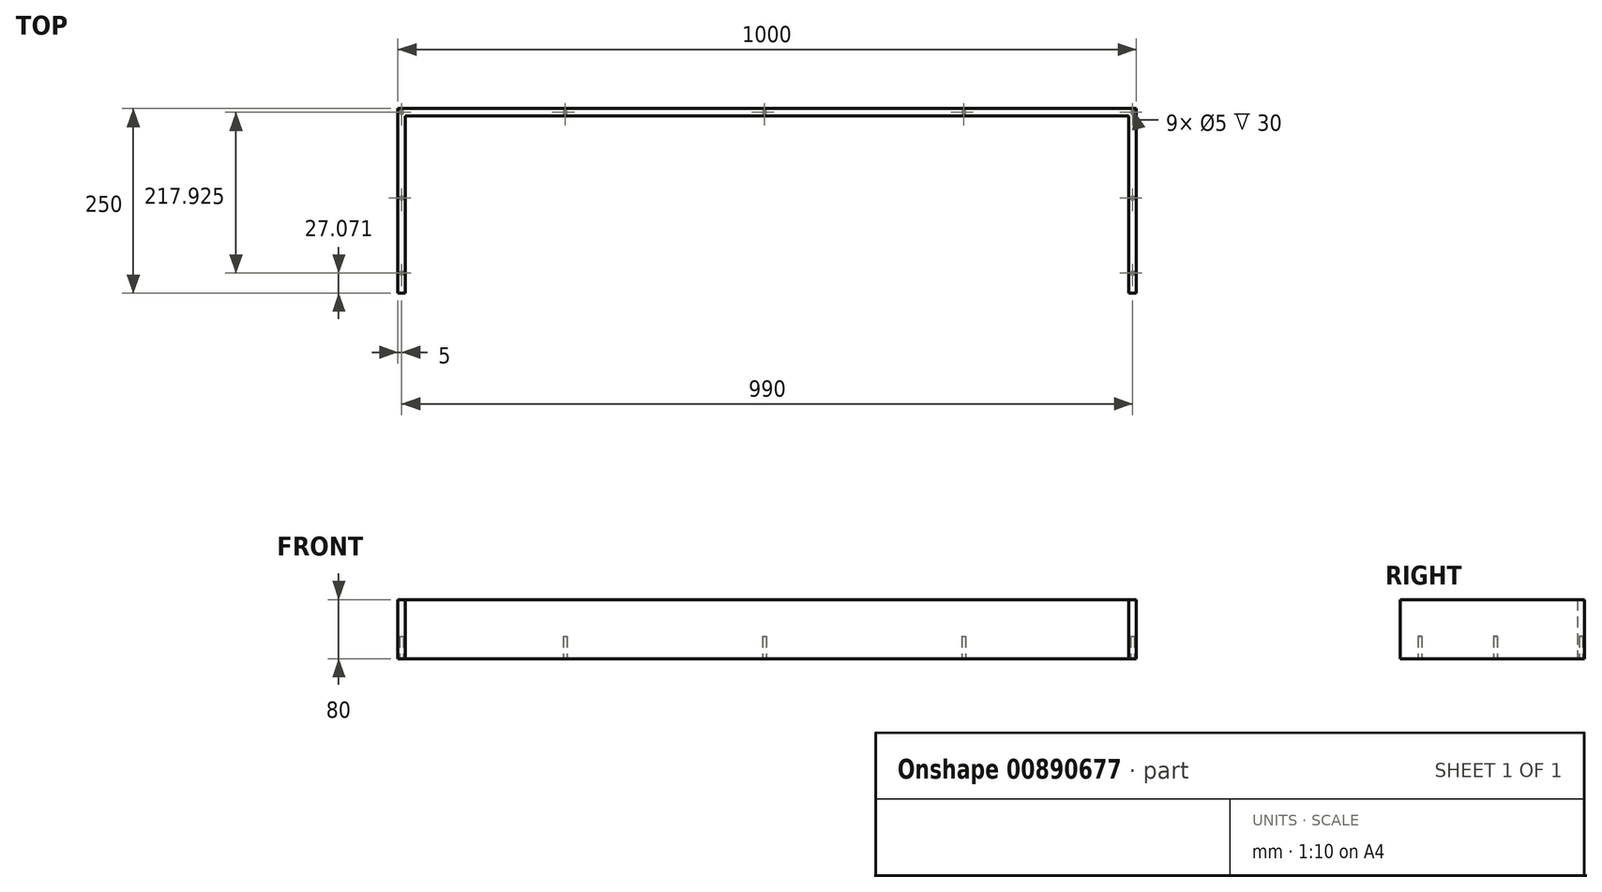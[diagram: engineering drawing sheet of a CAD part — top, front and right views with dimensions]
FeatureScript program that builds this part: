
annotation { "Feature Type Name" : "Feature", "Feature Type Description" : "" }
export const myFeature = defineFeature(function(context is Context, id is Id, definition is map)
    precondition{}
    {
        {
            var Q0;
            Q0=qCreatedBy(makeId("Top.planeOp"),FACE);
            var sketch = newSketch(context, id + "F0", { "sketchPlane" : qUnion([Q0])});
            skLineSegment(sketch, "E0.bottom", {"start": v(-496.42, 69.09) * mm, "end": v(503.58, 69.09) * mm});
            skLineSegment(sketch, "E0.top", {"start": v(-496.42, 59.09) * mm, "end": v(503.58, 59.09) * mm});
            skLineSegment(sketch, "E0.left", {"start": v(-496.42, 69.09) * mm, "end": v(-496.42, 59.09) * mm});
            skLineSegment(sketch, "E0.right", {"start": v(503.58, 69.09) * mm, "end": v(503.58, 59.09) * mm});
            skLineSegment(sketch, "E1.bottom", {"start": v(-496.42, 69.09) * mm, "end": v(-486.42, 69.09) * mm});
            skLineSegment(sketch, "E1.top", {"start": v(-496.42, -180.91) * mm, "end": v(-486.42, -180.91) * mm});
            skLineSegment(sketch, "E1.left", {"start": v(-496.42, 69.09) * mm, "end": v(-496.42, -180.91) * mm});
            skLineSegment(sketch, "E1.right", {"start": v(-486.42, 69.09) * mm, "end": v(-486.42, -180.91) * mm});
            skLineSegment(sketch, "E2.bottom", {"start": v(503.58, 69.09) * mm, "end": v(493.58, 69.09) * mm});
            skLineSegment(sketch, "E2.top", {"start": v(503.58, -180.91) * mm, "end": v(493.58, -180.91) * mm});
            skLineSegment(sketch, "E2.left", {"start": v(503.58, 69.09) * mm, "end": v(503.58, -180.91) * mm});
            skLineSegment(sketch, "E2.right", {"start": v(493.58, 69.09) * mm, "end": v(493.58, -180.91) * mm});
            skSolve(sketch);
        }
        {
            var Q0;
            Q0 = qSketchRegion(id + "F0", true);
            extrude(context, id + "F1", {"entities" : qUnion([Q0]), "depth" : 80 * mm, "offsetDistance" : 25 * mm});
        }
        {
            var Q0;
            Q0=makeQuery(id+"F1.opExtrude","CAP_FACE",FACE,{"disambiguationData":[OSD([sQuery(id+"F0.wireOp",EDGE,"E0.bottom"),sQuery(id+"F0.wireOp",EDGE,"E0.top"),sQuery(id+"F0.wireOp",EDGE,"E1.bottom"),sQuery(id+"F0.wireOp",EDGE,"E1.top"),sQuery(id+"F0.wireOp",EDGE,"E1.left"),sQuery(id+"F0.wireOp",EDGE,"E1.right"),sQuery(id+"F0.wireOp",EDGE,"E2.bottom"),sQuery(id+"F0.wireOp",EDGE,"E2.top"),sQuery(id+"F0.wireOp",EDGE,"E2.left"),sQuery(id+"F0.wireOp",EDGE,"E2.right")])],"isStart":true});
            var sketch = newSketch(context, id + "F2", { "sketchPlane" : qUnion([Q0])});
            skLineSegment(sketch, "E3", {"start": v(-491.42, 180.91) * mm, "end": v(-491.42, -76.7) * mm, "construction": true});
            skCircle(sketch, "E4", {"center": v(-491.42, 153.84) * mm, "radius": 2.5 * mm});
            skCircle(sketch, "E5", {"center": v(-491.42, 52.1) * mm, "radius": 2.5 * mm});
            skLineSegment(sketch, "E6", {"start": v(0, -69.09) * mm, "end": v(0, -59.09) * mm, "construction": true});
            skPoint(sketch, "E7", {"position": v(0, -64.09) * mm});
            skLineSegment(sketch, "E8", {"start": v(0, -64.09) * mm, "end": v(-568.45, -64.09) * mm, "construction": true});
            skCircle(sketch, "E9", {"center": v(-491.42, -64.09) * mm, "radius": 2.5 * mm});
            skCircle(sketch, "E10", {"center": v(-269.97, -64.09) * mm, "radius": 2.5 * mm});
            skCircle(sketch, "E11", {"center": v(0, -64.09) * mm, "radius": 2.5 * mm});
            skLineSegment(sketch, "E12", {"start": v(0, 55.46) * mm, "end": v(0, -93.93) * mm, "construction": true});
            skCircle(sketch, "E13.MirrorC", {"center": v(269.97, -64.09) * mm, "radius": 2.5 * mm});
            skLineSegment(sketch, "E14", {"start": v(269.97, -64.09) * mm, "end": v(528.6, -64.09) * mm, "construction": true});
            skCircle(sketch, "E15", {"center": v(498.58, -64.09) * mm, "radius": 2.5 * mm});
            skCircle(sketch, "E16", {"center": v(498.58, 52.1) * mm, "radius": 2.5 * mm});
            skCircle(sketch, "E17", {"center": v(498.58, 153.84) * mm, "radius": 2.5 * mm});
            skSolve(sketch);
        }
        {
            var Q0;
            Q0 = qSketchRegion(id + "F2", true);
            extrude(context, id + "F3", {"entities" : qUnion([Q0]), "operationType" : NewBodyOperationType.REMOVE, "oppositeDirection" : true, "depth" : 30 * mm, "offsetDistance" : 25 * mm});
        }
    });
